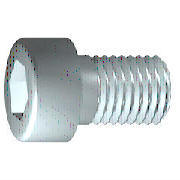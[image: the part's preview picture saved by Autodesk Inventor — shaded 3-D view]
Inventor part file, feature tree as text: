
AUTODESK INVENTOR PART (.ipt)
format: ipt  version: 2020 (Build 240168000, 168)  size: 201,728 bytes
history: native  units: mm (DEFAULTED — no unit token found)
features: sketch x2, other x1, extrude x1, plane x1, fillet x1
ambient origin geometry x7: Origin, YZ Plane, XY Plane, X Axis, Y Axis, Z Axis, Center Point
bodies: Solid1 (feature_tree)
feature tree (6):
  other  "Bryła"
  extrude  "Szczelina"  Depth=3.5mm
  plane  "Work Plane1"
  fillet  "Fillet2"  Radius=0.306825mm
  sketch  "Szkic1"
  sketch  "Szkic2"
